# Revit family: Bath-Drain-KOHLER-VOLUTE-K-18669T_1
name_source: partatom
category: Plumbing Fixtures
revit_build: Autodesk Revit 2017 (Build: 20160225_1515(x64)
units: mm (PartAtom-declared; Revit-internal decimal feet)

## family parameters
Cut with Voids When Loaded = No
Host = Face
OmniClass Number = 23.39.29.11
OmniClass Title = Waste Water Drains
Part Type = Normal
Room Calculation Point = No
Round Connector Dimension = Use Diameter
Shared = No

## types (1)
- CP-Polished Chrome
    ADA Compliant = No
    Assembly Code = D2010500
    CW Connection = Yes
    Cold Water Inlet = Cold Water Inlet
    Date Modified = 03/03/2021
    Default Elevation = 0"
    Description = Fule three-in-one bathtub drain
    Finish = Kohler-Metal-CP-Polished_Chrome
    Flow Rate = 16 GPM
    HW Connection = No
    Height = 19 15/16"
    Hot Water Inlet = Hot Water Inlet
    Length = 11 9/16"
    Manufacturer = KOHLER Co.
    Master Format 2014 = 22 13 19.13
    Master Format 2014 Name = Sanitary Drains
    Material = Premium Metal Construction
    Model = K-18669T-CP
    Pressure = 0.00 psi
    Product Documentation Link = https://files.kohler.com.cn
    Product Name = VOLUTE
    Product Page URL = https://www.kohler.com.cn
    Type = 1
    URL = http://www.kohler.com.cn
    Vent Connection = No
    Waste Connection = Yes
    Waste Water Outlet = Waste Water Outlet
    WaterSense Certified = No
    Width = 17 3/8"

## geometry (parser evidence)
native form markers: Sweep x6
no freeform markers — native parametric forms only
